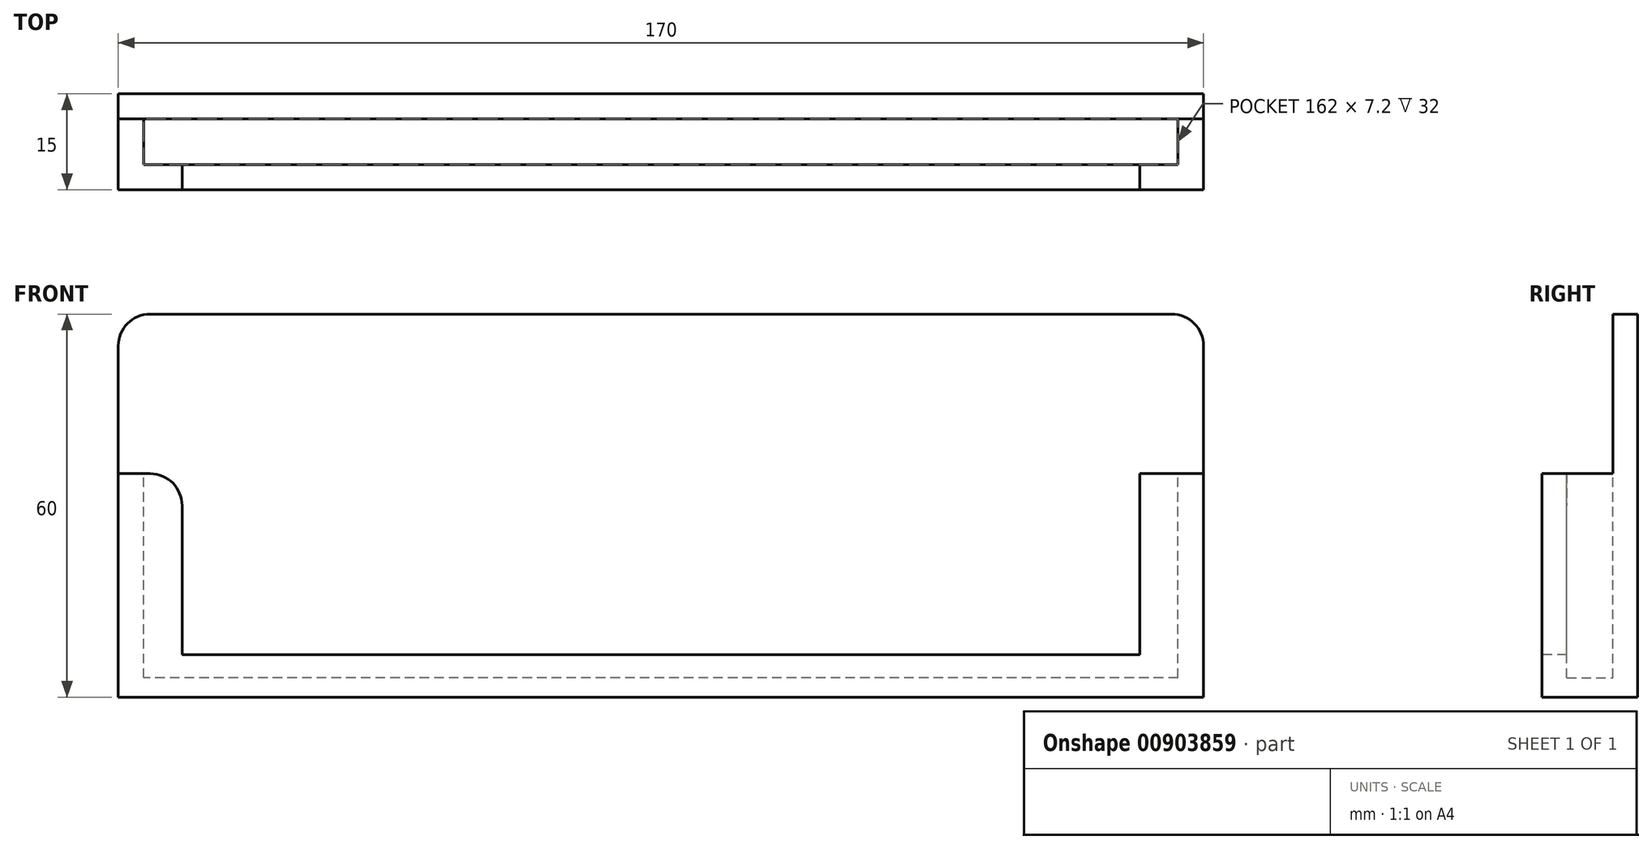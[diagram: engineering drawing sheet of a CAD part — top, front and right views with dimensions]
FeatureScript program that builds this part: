
annotation { "Feature Type Name" : "Feature", "Feature Type Description" : "" }
export const myFeature = defineFeature(function(context is Context, id is Id, definition is map)
    precondition{}
    {
        {
            var Q0;
            Q0=qCreatedBy(makeId("Front.planeOp"),FACE);
            var sketch = newSketch(context, id + "F0", { "sketchPlane" : qUnion([Q0])});
            skLineSegment(sketch, "E0.bottom", {"start": v(85, -17.5) * mm, "end": v(-85, -17.5) * mm});
            skLineSegment(sketch, "E0.top", {"start": v(85, 17.5) * mm, "end": v(-85, 17.5) * mm});
            skLineSegment(sketch, "E0.left", {"start": v(85, -17.5) * mm, "end": v(85, 17.5) * mm});
            skLineSegment(sketch, "E0.right", {"start": v(-85, -17.5) * mm, "end": v(-85, 17.5) * mm});
            skPoint(sketch, "E0.middle", {"position": v(0, 0) * mm});
            skSolve(sketch);
        }
        {
            var Q0;
            Q0 = qSketchRegion(id + "F0", true);
            extrude(context, id + "F1", {"entities" : qUnion([Q0]), "depth" : 15 * mm, "offsetDistance" : 25 * mm});
        }
        {
            var Q0;
            Q0=makeQuery(id+"F1.opExtrude","SWEPT_FACE",FACE,{"disambiguationData":[OSD([sQuery(id+"F0.wireOp",EDGE,"E0.top")])]});
            var sketch = newSketch(context, id + "F2", { "sketchPlane" : qUnion([Q0])});
            skLineSegment(sketch, "E1.bottom", {"start": v(81, -11.1) * mm, "end": v(-81, -11.1) * mm});
            skLineSegment(sketch, "E1.top", {"start": v(81, -3.9) * mm, "end": v(-81, -3.9) * mm});
            skLineSegment(sketch, "E1.left", {"start": v(81, -11.1) * mm, "end": v(81, -3.9) * mm});
            skLineSegment(sketch, "E1.right", {"start": v(-81, -11.1) * mm, "end": v(-81, -3.9) * mm});
            skPoint(sketch, "E1.middle", {"position": v(0, -7.5) * mm});
            skPoint(sketch, "E1.middle.positionSnap0", {"position": v(85, -7.5) * mm});
            skPoint(sketch, "E1.middle.positionSnap1", {"position": v(0, -15) * mm});
            skPoint(sketch, "E1.centerSnap0", {"position": v(85, -7.5) * mm});
            skPoint(sketch, "E1.centerSnap1", {"position": v(0, -15) * mm});
            skSolve(sketch);
        }
        {
            var Q0;
            Q0 = qSketchRegion(id + "F2", true);
            extrude(context, id + "F3", {"entities" : qUnion([Q0]), "operationType" : NewBodyOperationType.REMOVE, "oppositeDirection" : true, "depth" : 32 * mm, "offsetDistance" : 25 * mm});
        }
        {
            var Q0;
            Q0=makeQuery(id+"F1.opExtrude","SWEPT_FACE",FACE,{"disambiguationData":[OSD([sQuery(id+"F0.wireOp",EDGE,"E0.top")])]});
            var sketch = newSketch(context, id + "F4", { "sketchPlane" : qUnion([Q0])});
            skLineSegment(sketch, "E2.bottom", {"start": v(-85, 0) * mm, "end": v(85, 0) * mm});
            skLineSegment(sketch, "E2.top", {"start": v(-85, -3.9) * mm, "end": v(85, -3.9) * mm});
            skLineSegment(sketch, "E2.left", {"start": v(-85, 0) * mm, "end": v(-85, -3.9) * mm});
            skLineSegment(sketch, "E2.right", {"start": v(85, 0) * mm, "end": v(85, -3.9) * mm});
            skSolve(sketch);
        }
        {
            var Q0;
            Q0 = qSketchRegion(id + "F4", true);
            extrude(context, id + "F5", {"entities" : qUnion([Q0]), "operationType" : NewBodyOperationType.ADD, "depth" : 25 * mm, "offsetDistance" : 25 * mm});
        }
        {
            var Q0;
            Q0=makeQuery(id+"F1.opExtrude","CAP_FACE",FACE,{"disambiguationData":[OSD([sQuery(id+"F0.wireOp",EDGE,"E0.bottom"),sQuery(id+"F0.wireOp",EDGE,"E0.top"),sQuery(id+"F0.wireOp",EDGE,"E0.left"),sQuery(id+"F0.wireOp",EDGE,"E0.right")])],"isStart":false});
            var sketch = newSketch(context, id + "F6", { "sketchPlane" : qUnion([Q0])});
            skLineSegment(sketch, "E3.bottom", {"start": v(-75, 17.5) * mm, "end": v(75, 17.5) * mm});
            skLineSegment(sketch, "E3.top", {"start": v(-75, -10.87) * mm, "end": v(75, -10.87) * mm});
            skLineSegment(sketch, "E3.left", {"start": v(-75, 17.5) * mm, "end": v(-75, -10.87) * mm});
            skLineSegment(sketch, "E3.right", {"start": v(75, 17.5) * mm, "end": v(75, -10.87) * mm});
            skSolve(sketch);
        }
        {
            var Q0;
            Q0 = qSketchRegion(id + "F6", true);
            extrude(context, id + "F7", {"entities" : qUnion([Q0]), "operationType" : NewBodyOperationType.REMOVE, "oppositeDirection" : true, "depth" : 6.3 * mm, "offsetDistance" : 25 * mm});
        }
        {
            var Q0;
            Q0=makeQuery(id+"F5.opExtrude","CAP_EDGE",EDGE,{"disambiguationData":[OSD([sQuery(id+"F4.wireOp",EDGE,"E2.left")])],"isStart":false});
            var Q1;
            Q1=makeQuery(id+"F5.opExtrude","CAP_EDGE",EDGE,{"disambiguationData":[OSD([sQuery(id+"F4.wireOp",EDGE,"E2.right")])],"isStart":false});
            var Q2;
            Q2=makeQuery(id+"F7.boolean.opBoolean","COPY",EDGE,{"derivedFrom":makeQuery(id+"F7.opExtrude","SWEPT_EDGE",EDGE,{"disambiguationData":[OSD([sQuery(id+"F0.wireOp",EDGE,"E0.top"),sQuery(id+"F6.wireOp",EDGE,"E3.bottom"),sQuery(id+"F6.wireOp",EDGE,"E3.right")])]})});
            var Q3;
            Q3=makeQuery(id+"F7.boolean.opBoolean","COPY",EDGE,{"derivedFrom":makeQuery(id+"F7.opExtrude","SWEPT_EDGE",EDGE,{"disambiguationData":[OSD([sQuery(id+"F0.wireOp",EDGE,"E0.top"),sQuery(id+"F6.wireOp",EDGE,"E3.bottom"),sQuery(id+"F6.wireOp",EDGE,"E3.left")])]})});
            fillet(context, id + "F8", {"entities" : qUnion([Q0, Q1, Q2, Q3]), "radius" : 5 * mm, "tangentPropagation" : true, "allowEdgeOverflow" : false});
        }
    });
